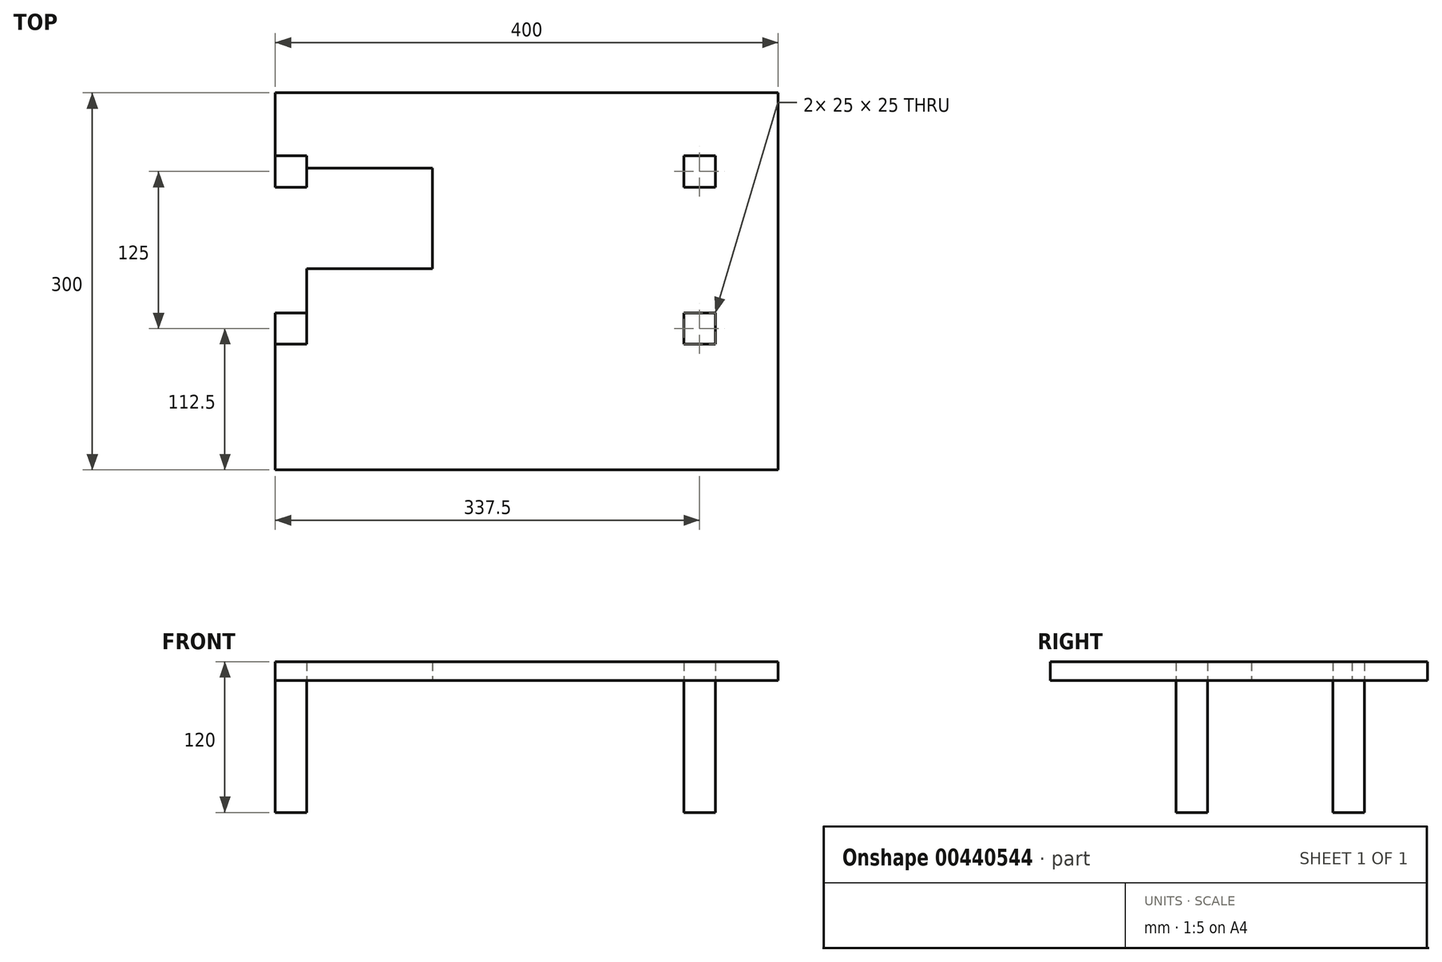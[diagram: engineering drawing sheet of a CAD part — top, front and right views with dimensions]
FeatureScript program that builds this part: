
annotation { "Feature Type Name" : "Feature", "Feature Type Description" : "" }
export const myFeature = defineFeature(function(context is Context, id is Id, definition is map)
    precondition{}
    {
        {
            var Q0;
            Q0=qCreatedBy(makeId("Top.planeOp"),FACE);
            var sketch = newSketch(context, id + "F0", { "sketchPlane" : qUnion([Q0])});
            skLineSegment(sketch, "E0.bottom", {"start": v(-200, 150) * mm, "end": v(200, 150) * mm});
            skLineSegment(sketch, "E0.top", {"start": v(-200, -150) * mm, "end": v(200, -150) * mm});
            skLineSegment(sketch, "E0.right", {"start": v(200, 150) * mm, "end": v(200, -150) * mm});
            skPoint(sketch, "E0.middle", {"position": v(0, 0) * mm});
            skLineSegment(sketch, "E1", {"start": v(-200, 100) * mm, "end": v(-175, 100) * mm});
            skLineSegment(sketch, "E2", {"start": v(-200, -50) * mm, "end": v(-175, -50) * mm});
            skLineSegment(sketch, "E3", {"start": v(-200, -25) * mm, "end": v(-175, -25) * mm});
            skLineSegment(sketch, "E4", {"start": v(-200, 75) * mm, "end": v(-175, 75) * mm});
            skLineSegment(sketch, "E5", {"start": v(-175, 100) * mm, "end": v(-175, 75) * mm});
            skLineSegment(sketch, "E6", {"start": v(-175, -25) * mm, "end": v(-175, -50) * mm});
            skLineSegment(sketch, "E7", {"start": v(150, 100) * mm, "end": v(125, 100) * mm});
            skLineSegment(sketch, "E8", {"start": v(125, 75) * mm, "end": v(150, 75) * mm});
            skLineSegment(sketch, "E9", {"start": v(125, -25) * mm, "end": v(150, -25) * mm});
            skLineSegment(sketch, "E10", {"start": v(125, -50) * mm, "end": v(150, -50) * mm});
            skLineSegment(sketch, "E11", {"start": v(125, 100) * mm, "end": v(125, 75) * mm});
            skLineSegment(sketch, "E12", {"start": v(125, -25) * mm, "end": v(125, -50) * mm});
            skLineSegment(sketch, "E13", {"start": v(150, -50) * mm, "end": v(150, -25) * mm});
            skLineSegment(sketch, "E14", {"start": v(150, 100) * mm, "end": v(150, 75) * mm});
            skLineSegment(sketch, "E15", {"start": v(-75, 90) * mm, "end": v(-160, 90) * mm});
            skLineSegment(sketch, "E16", {"start": v(-160, 10) * mm, "end": v(-75, 10) * mm});
            skLineSegment(sketch, "E17", {"start": v(-75, 90) * mm, "end": v(-75, 10) * mm});
            skLineSegment(sketch, "E18", {"start": v(-200, -25) * mm, "end": v(-200, -50) * mm});
            skLineSegment(sketch, "E19", {"start": v(-200, -150) * mm, "end": v(-200, -50) * mm});
            skLineSegment(sketch, "E20", {"start": v(-200, 75) * mm, "end": v(-200, 100) * mm});
            skLineSegment(sketch, "E21", {"start": v(-200, 150) * mm, "end": v(-200, 100) * mm});
            skLineSegment(sketch, "E22", {"start": v(-160, 10) * mm, "end": v(-175, 10) * mm});
            skLineSegment(sketch, "E23", {"start": v(-160, 90) * mm, "end": v(-175, 90) * mm});
            skLineSegment(sketch, "E24", {"start": v(-175, 10) * mm, "end": v(-175, -25) * mm});
            skSolve(sketch);
        }
        {
            var Q0;
            {var subQ3=sQuery(id+"F0.wireOp",EDGE,"E0.bottom");Q0=makeQuery(id+"F0.imprint","IMPRINT",FACE,{"disambiguationData":[TD([[makeQuery(id+"F0.imprint","IMPRINT",EDGE,{"derivedFrom":subQ3}),-1.0]])]});}
            extrude(context, id + "F1", {"entities" : qUnion([Q0]), "depth" : 15 * mm});
        }
        {
            var Q0;
            {var subQ0=sQuery(id+"F0.wireOp",EDGE,"E1");Q0=makeQuery(id+"F0.imprint","IMPRINT",FACE,{"disambiguationData":[TD([[makeQuery(id+"F0.imprint","IMPRINT",EDGE,{"derivedFrom":subQ0}),-1.0]])]});}
            var Q1;
            {var subQ0=sQuery(id+"F0.wireOp",EDGE,"E2");Q1=makeQuery(id+"F0.imprint","IMPRINT",FACE,{"disambiguationData":[TD([[makeQuery(id+"F0.imprint","IMPRINT",EDGE,{"derivedFrom":subQ0}),1.0]])]});}
            var Q2;
            Q2=makeQuery(id+"F0.imprint","IMPRINT",FACE,{"disambiguationData":[TD([[makeQuery(id+"F0.imprint","IMPRINT",EDGE,{"derivedFrom":sQuery(id+"F0.wireOp",EDGE,"E9")}),-1.0]])]});
            var Q3;
            Q3=makeQuery(id+"F0.imprint","IMPRINT",FACE,{"disambiguationData":[TD([[makeQuery(id+"F0.imprint","IMPRINT",EDGE,{"derivedFrom":sQuery(id+"F0.wireOp",EDGE,"E7")}),1.0]])]});
            extrude(context, id + "F2", {"entities" : qUnion([Q0, Q1, Q2, Q3]), "oppositeDirection" : true, "depth" : 105 * mm});
        }
        {
            var Q0;
            Q0=makeQuery(id+"F0.imprint","IMPRINT",FACE,{"disambiguationData":[TD([[makeQuery(id+"F0.imprint","IMPRINT",EDGE,{"derivedFrom":sQuery(id+"F0.wireOp",EDGE,"E7")}),1.0]])]});
            var Q1;
            Q1=makeQuery(id+"F0.imprint","IMPRINT",FACE,{"disambiguationData":[TD([[makeQuery(id+"F0.imprint","IMPRINT",EDGE,{"derivedFrom":sQuery(id+"F0.wireOp",EDGE,"E9")}),-1.0]])]});
            var Q2;
            {var subQ0=sQuery(id+"F0.wireOp",EDGE,"E2");Q2=makeQuery(id+"F0.imprint","IMPRINT",FACE,{"disambiguationData":[TD([[makeQuery(id+"F0.imprint","IMPRINT",EDGE,{"derivedFrom":subQ0}),1.0]])]});}
            var Q3;
            {var subQ0=sQuery(id+"F0.wireOp",EDGE,"E1");Q3=makeQuery(id+"F0.imprint","IMPRINT",FACE,{"disambiguationData":[TD([[makeQuery(id+"F0.imprint","IMPRINT",EDGE,{"derivedFrom":subQ0}),-1.0]])]});}
            extrude(context, id + "F3", {"entities" : qUnion([Q0, Q1, Q2, Q3]), "depth" : 15 * mm});
        }
    });
